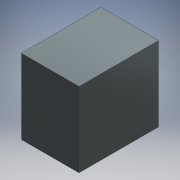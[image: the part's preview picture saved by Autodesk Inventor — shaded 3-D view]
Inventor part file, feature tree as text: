
AUTODESK INVENTOR PART (.ipt)
format: ipt  version: 2016 (Build 200138000, 138)  size: 172,032 bytes
history: native  units: mm
features: extrude x6, sketch x6
ambient origin geometry x8: Origin, YZ Plane, XZ Plane, XY Plane, X Axis, Y Axis, Z Axis, Center Point
bodies: Body1 (feature_tree)
feature tree (12):
  extrude  "Extrusion2"  Depth=548.0mm
  extrude  "Extrusion3"  Depth=583.0mm TaperAngle=0.0deg
  extrude  "Extrusion4"  Depth=345.0mm
  extrude  "Extrusion5"  Depth=88.0mm
  extrude  "Extrusion6"  Depth=75.0mm
  extrude  "Extrusion7"  Depth=583.0mm TaperAngle=0.0deg
  sketch  "Sketch1"  dims[d0=422.0mm d1=548.0mm]
  sketch  "Sketch2"  dims[d4=23.0mm d5=583.0mm d6=0.0mm]
  sketch  "Sketch3"  dims[d7=210.0mm d8=345.0mm]
  sketch  "Sketch4"  dims[d9=88.0mm d11=88.0mm]
  sketch  "Sketch5"  dims[d12=583.0mm d13=0.0mm d14=75.0mm]
  sketch  "Sketch6"  dims[d15=104.0mm d16=583.0mm d17=0.0mm d18=54.0mm d19=583.0mm d20=0.0mm d21=16.0mm d22=16.0mm d23=170.0mm d24=200.0mm d25=45.0mm d26=45.0mm d27=170.0mm d28=200.0mm d29=16.0mm d30=16.0mm d31=45.0mm d32=45.0mm d33=16.0mm d34=0.0mm d35=123.0mm d36=0.0mm]
